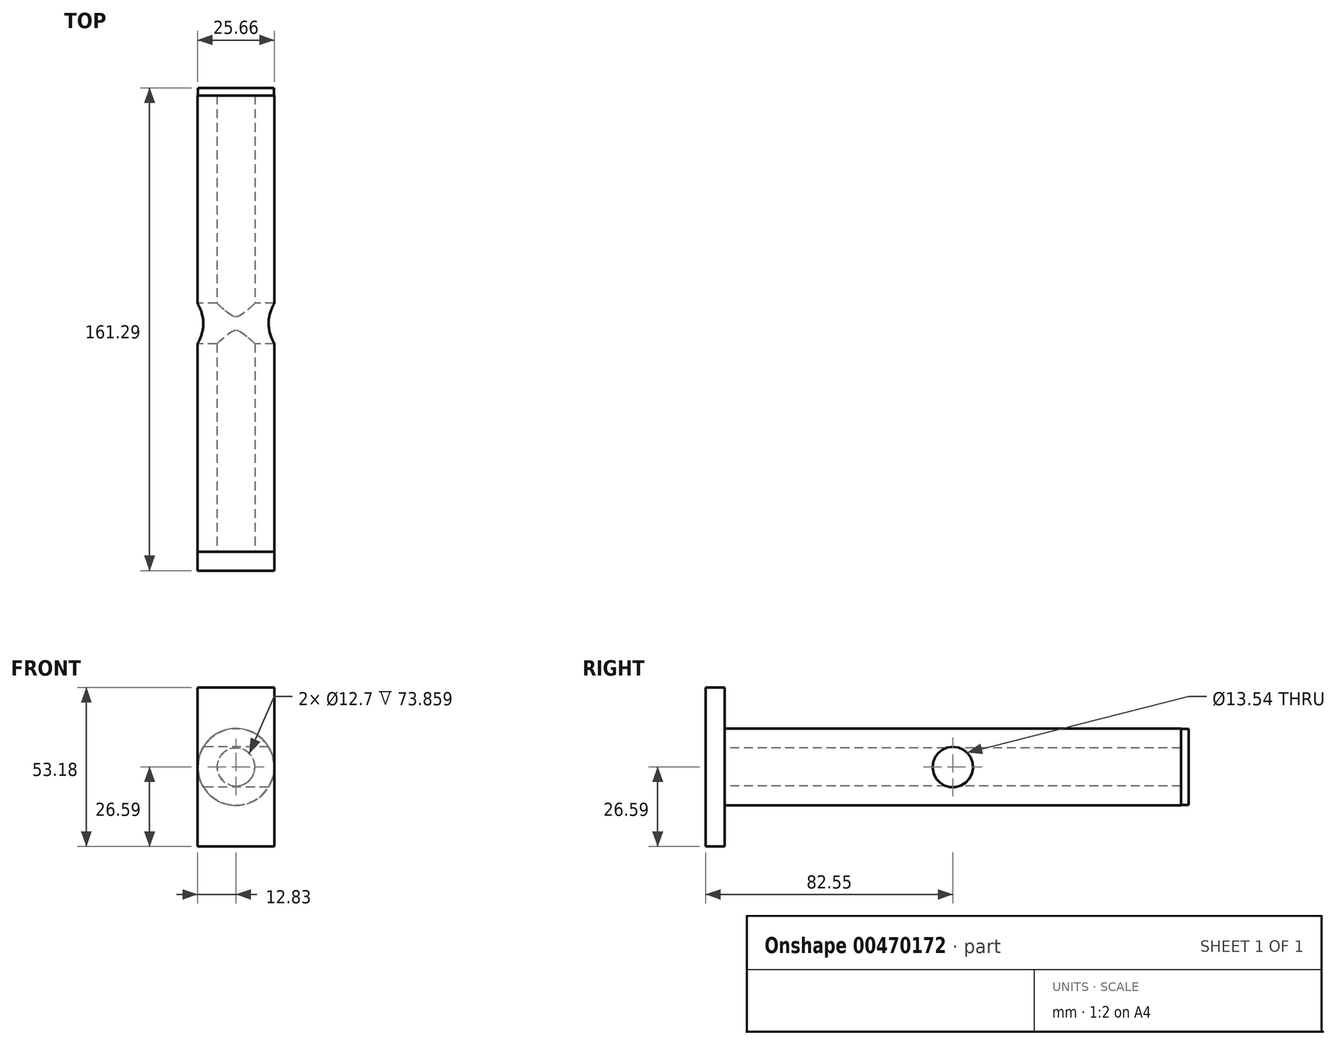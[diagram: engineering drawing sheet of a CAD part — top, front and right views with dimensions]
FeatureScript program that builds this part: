
annotation { "Feature Type Name" : "Feature", "Feature Type Description" : "" }
export const myFeature = defineFeature(function(context is Context, id is Id, definition is map)
    precondition{}
    {
        {
            var Q0;
            Q0=qCreatedBy(makeId("Front.planeOp"),FACE);
            cPlane(context, id + "F0", {"entities" : qUnion([Q0]), "cplaneType" : CPlaneType.OFFSET, "offset" : 76.2 * mm, "width" : 152.4 * mm, "height" : 152.4 * mm});
        }
        {
            var Q0;
            Q0=qCreatedBy(makeId("Front.planeOp"),FACE);
            var sketch = newSketch(context, id + "F1", { "sketchPlane" : qUnion([Q0])});
            skCircle(sketch, "E0", {"center": v(0, 0) * mm, "radius": 12.83 * mm});
            skSolve(sketch);
        }
        {
            var Q0;
            Q0 = qSketchRegion(id + "F1", true);
            extrude(context, id + "F2", {"entities" : qUnion([Q0]), "depth" : 76.2 * mm, "hasSecondDirection" : true, "secondDirectionOppositeDirection" : true, "secondDirectionDepth" : 76.2 * mm});
        }
        {
            var Q0;
            Q0=sQuery(id+"F1.wireOp",VERTEX,"E0.center");
            var Q1;
            Q1=makeQuery(id+"F2.opExtrude","SWEPT_BODY",BODY,{"disambiguationData":[OSD([sQuery(id+"F1.wireOp",EDGE,"E0")])]});
            hole(context, id + "F3", {"style" : HoleStyle.SIMPLE, "endStyle" : HoleEndStyle.THROUGH, "holeDiameter" : 12.7 * mm, "isTappedThrough" : true, "tappedDepth" : 12.7 * mm, "tapClearance" : 3, "locations" : qUnion([Q0]), "scope" : qUnion([Q1])});
        }
        {
            var Q0;
            Q0=sQuery(id+"F1.wireOp",VERTEX,"E0.center");
            var Q1;
            Q1=makeQuery(id+"F2.opExtrude","SWEPT_BODY",BODY,{"disambiguationData":[OSD([sQuery(id+"F1.wireOp",EDGE,"E0")])]});
            hole(context, id + "F4", {"style" : HoleStyle.SIMPLE, "endStyle" : HoleEndStyle.THROUGH, "oppositeDirection" : true, "holeDiameter" : 12.7 * mm, "isTappedThrough" : true, "tappedDepth" : 12.7 * mm, "tapClearance" : 3, "locations" : qUnion([Q0]), "scope" : qUnion([Q1])});
        }
        {
            var Q0;
            Q0=qCreatedBy(id+"F0.planeOp",FACE);
            var sketch = newSketch(context, id + "F5", { "sketchPlane" : qUnion([Q0])});
            skLineSegment(sketch, "E1.bottom", {"start": v(12.8, 26.59) * mm, "end": v(-12.8, 26.59) * mm});
            skLineSegment(sketch, "E1.top", {"start": v(12.8, -26.59) * mm, "end": v(-12.8, -26.59) * mm});
            skLineSegment(sketch, "E1.left", {"start": v(12.8, 26.59) * mm, "end": v(12.8, -26.59) * mm});
            skLineSegment(sketch, "E1.right", {"start": v(-12.8, 26.59) * mm, "end": v(-12.8, -26.59) * mm});
            skPoint(sketch, "E1.middle", {"position": v(0, 0) * mm});
            skSolve(sketch);
        }
        {
            var Q0;
            Q0 = qSketchRegion(id + "F5", true);
            extrude(context, id + "F6", {"entities" : qUnion([Q0]), "operationType" : NewBodyOperationType.ADD, "depth" : 6.35 * mm});
        }
        {
            var Q0;
            Q0=qCreatedBy(makeId("Front.planeOp"),FACE);
            cPlane(context, id + "F7", {"entities" : qUnion([Q0]), "cplaneType" : CPlaneType.OFFSET, "offset" : 76.2 * mm, "oppositeDirection" : true, "width" : 152.4 * mm, "height" : 152.4 * mm});
        }
        {
            var Q0;
            Q0=qCreatedBy(id+"F7.planeOp",FACE);
            var sketch = newSketch(context, id + "F8", { "sketchPlane" : qUnion([Q0])});
            skCircle(sketch, "E2", {"center": v(0, 0) * mm, "radius": 12.7 * mm});
            skSolve(sketch);
        }
        {
            var Q0;
            Q0 = qSketchRegion(id + "F8", true);
            extrude(context, id + "F9", {"entities" : qUnion([Q0]), "operationType" : NewBodyOperationType.ADD, "oppositeDirection" : true, "depth" : 2.54 * mm});
        }
        {
            var Q0;
            Q0=qCreatedBy(makeId("Right.planeOp"),FACE);
            var sketch = newSketch(context, id + "F10", { "sketchPlane" : qUnion([Q0])});
            skCircle(sketch, "E3", {"center": v(0, 0) * mm, "radius": 6.77 * mm});
            skSolve(sketch);
        }
        {
            var Q0;
            Q0=sQuery(id+"F10.wireOp",VERTEX,"E3.center");
            var Q1;
            Q1=makeQuery(id+"F2.opExtrude","SWEPT_BODY",BODY,{"disambiguationData":[OSD([sQuery(id+"F1.wireOp",EDGE,"E0")])]});
            hole(context, id + "F11", {"style" : HoleStyle.SIMPLE, "endStyle" : HoleEndStyle.THROUGH, "holeDiameter" : 6.35 * mm, "isTappedThrough" : true, "tappedDepth" : 12.7 * mm, "tapClearance" : 3, "locations" : qUnion([Q0]), "scope" : qUnion([Q1])});
        }
        {
            var Q0;
            Q0 = qSketchRegion(id + "F10", true);
            extrude(context, id + "F12", {"entities" : qUnion([Q0]), "operationType" : NewBodyOperationType.REMOVE, "depth" : 50.8 * mm, "hasSecondDirection" : true, "secondDirectionOppositeDirection" : true, "secondDirectionDepth" : 50.8 * mm});
        }
    });
